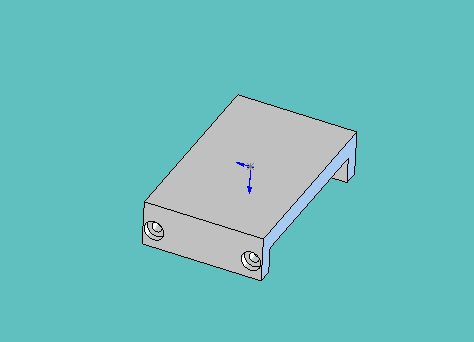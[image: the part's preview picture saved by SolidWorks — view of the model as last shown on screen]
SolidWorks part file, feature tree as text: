
SOLIDWORKS PART (.sldprt)
format: sldprt  version: not decoded by parser v0  size: 156,672 bytes
history: native  units: mm
features: sketch x5, cut_extrude x4, material x1, extrude x1 (+11 scaffold rows collapsed)
feature tree (22):
  scaffold x11  (default folders/planes/origin — collapsed)
  material  "Material <not specified>"
  sketch  "Sketch1"  dims[D5=~1.984375mm D1=23.368mm D2=9.525mm D3=9.017mm D4=5.4864mm]
  extrude  "Extrude1"  Depth=19.05mm
  sketch  "Sketch2"  dims[D2=31.9024mm D3=15.9512mm D1=0.0mm]
  cut_extrude  "Cut-Extrude1"  Depth=3.96875mm
  sketch  "Sketch3"  dims[D1=7.9375mm D2=7.9375mm]
  cut_extrude  "Cut-Extrude2"  Depth=1.27mm
  sketch  "Sketch4"  dims[D1=3.8608mm D2=3.8608mm]
  cut_extrude  "Cut-Extrude3"  Depth=1.27mm
  sketch  "Sketch5"
  cut_extrude  "Cut-Extrude4"  Depth=1.27mm
decode coverage: 9 of 10 modeling features carry decoded parameters
note: ~ marks probable driven/reference dimensions
note: suppression state not decoded; provenance and decode notes live in map.json
